# Revit family: BTC120
name_source: partatom
category: Structural Connections
revit_build: Autodesk Revit 2015 (Build: 20140606_1530(x64)
units: mm (PartAtom-declared; Revit-internal decimal feet)

## types (1)
- BTC120
    Default Elevation = 0 mm  [stored 0 ft]
    Density = 1.00 kg
    Description = Concealed beam hanger
    EPD = https://www.strongtie.eu
    ETA / DoP = https://www.strongtie.eu
    H = 120 mm  [stored 0.393701 ft]
    Manufacturer = Simpson Strong-Tie
    Model = BTC120
    Model Disclaimer = Contact Simpson Strong-Tie Company  for more information
    Model ID = 0005747776674903005703466647814376444818
    Name = BTC120
    ObjectType = BTC120
    Product Material = Galvanised
    Product Type = Concealed beam hanger
    Reference = BTC120-B
    STD type1 = STD12X60
    STD type2 = STD12X80
    STD type3 = STD12X100
    STD type4 = STD12X120
    STD type5 = STD12X140
    STD type6 = STD12X160
    STD type7 = STD12X180
    Technical datasheet = https://www.strongtie.eu
    URL = www.strongtie.eu
    UniClass Number = Pr_20_29_31_13
    UniClass Title = Carbon steel punched metal plate fasteners
    W = 96 mm  [stored 0.314961 ft]

note: [stored X ft] marks values corroborated as IEEE doubles in the binary element streams (Revit-internal decimal feet)

## geometry (parser evidence)
native form markers: Blend x70, Sweep x12
no freeform markers — native parametric forms only
